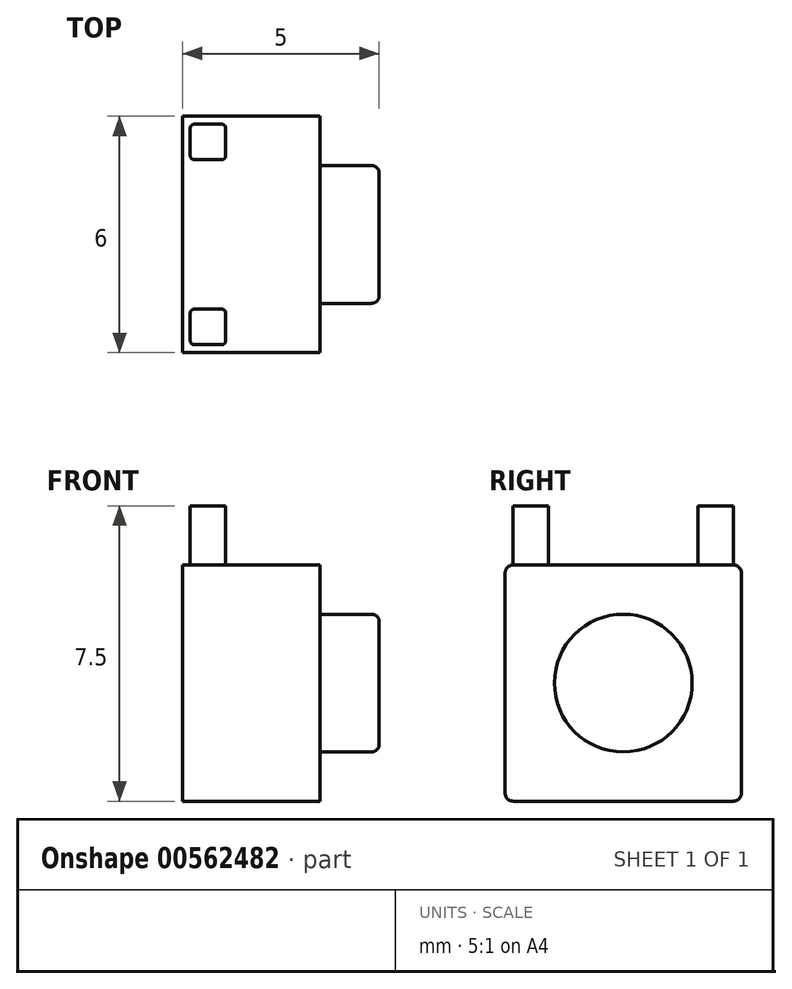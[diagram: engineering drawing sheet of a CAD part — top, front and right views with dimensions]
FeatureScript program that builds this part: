
annotation { "Feature Type Name" : "Feature", "Feature Type Description" : "" }
export const myFeature = defineFeature(function(context is Context, id is Id, definition is map)
    precondition{}
    {
        {
            var Q0;
            Q0=qCreatedBy(makeId("Right.planeOp"),FACE);
            var sketch = newSketch(context, id + "F0", { "sketchPlane" : qUnion([Q0])});
            skLineSegment(sketch, "E0.bottom", {"start": v(-3, 3) * mm, "end": v(3, 3) * mm});
            skLineSegment(sketch, "E0.top", {"start": v(-3, -3) * mm, "end": v(3, -3) * mm});
            skLineSegment(sketch, "E0.left", {"start": v(-3, 3) * mm, "end": v(-3, -3) * mm});
            skLineSegment(sketch, "E0.right", {"start": v(3, 3) * mm, "end": v(3, -3) * mm});
            skPoint(sketch, "E0.middle", {"position": v(0, 0) * mm});
            skSolve(sketch);
        }
        {
            var Q0;
            Q0=qSketchRegion(id+"F0",true);
            extrude(context, id + "F1", {"entities" : qUnion([Q0]), "depth" : 3.5 * mm, "offsetDistance" : 25 * mm, "symmetric" : true});
        }
        {
            var Q0;
            Q0=makeQuery(id+"F1.opExtrude","CAP_FACE",FACE,{"disambiguationData":[OSD([sQuery(id+"F0.wireOp",EDGE,"E0.bottom"),sQuery(id+"F0.wireOp",EDGE,"E0.top"),sQuery(id+"F0.wireOp",EDGE,"E0.left"),sQuery(id+"F0.wireOp",EDGE,"E0.right")])],"isStart":false});
            var sketch = newSketch(context, id + "F2", { "sketchPlane" : qUnion([Q0])});
            skCircle(sketch, "E1", {"center": v(0, 0) * mm, "radius": 1.75 * mm});
            skSolve(sketch);
        }
        {
            var Q0;
            Q0=makeQuery(id+"F2.imprint","IMPRINT",FACE,{"disambiguationData":[TD([[makeQuery(id+"F2.imprint","IMPRINT",EDGE,{"derivedFrom":sQuery(id+"F2.wireOp",EDGE,"E1")}),1.0]])]});
            extrude(context, id + "F3", {"entities" : qUnion([Q0]), "operationType" : NewBodyOperationType.ADD, "depth" : 1.5 * mm, "offsetDistance" : 25 * mm});
        }
        {
            var Q0;
            Q0=makeQuery(id+"F3.opExtrude","CAP_EDGE",EDGE,{"disambiguationData":[OSD([sQuery(id+"F2.wireOp",EDGE,"E1")])],"isStart":false});
            var Q1;
            Q1=makeQuery(id+"F1.opExtrude","SWEPT_EDGE",EDGE,{"disambiguationData":[OSD([sQuery(id+"F0.wireOp",EDGE,"E0.bottom"),sQuery(id+"F0.wireOp",EDGE,"E0.left")])]});
            var Q2;
            Q2=makeQuery(id+"F1.opExtrude","SWEPT_EDGE",EDGE,{"disambiguationData":[OSD([sQuery(id+"F0.wireOp",EDGE,"E0.bottom"),sQuery(id+"F0.wireOp",EDGE,"E0.right")])]});
            var Q3;
            Q3=makeQuery(id+"F1.opExtrude","SWEPT_EDGE",EDGE,{"disambiguationData":[OSD([sQuery(id+"F0.wireOp",EDGE,"E0.top"),sQuery(id+"F0.wireOp",EDGE,"E0.right")])]});
            var Q4;
            Q4=makeQuery(id+"F1.opExtrude","SWEPT_EDGE",EDGE,{"disambiguationData":[OSD([sQuery(id+"F0.wireOp",EDGE,"E0.top"),sQuery(id+"F0.wireOp",EDGE,"E0.left")])]});
            fillet(context, id + "F4", {"entities" : qUnion([Q0, Q1, Q2, Q3, Q4]), "radius" : .2 * mm, "tangentPropagation" : true, "allowEdgeOverflow" : false});
        }
        {
            var Q0;
            Q0=makeQuery(id+"F1.opExtrude","SWEPT_FACE",FACE,{"disambiguationData":[OSD([sQuery(id+"F0.wireOp",EDGE,"E0.bottom")])]});
            var sketch = newSketch(context, id + "F5", { "sketchPlane" : qUnion([Q0])});
            skLineSegment(sketch, "E2.bottom", {"start": v(-1.45, -2.8) * mm, "end": v(-0.75, -2.8) * mm});
            skLineSegment(sketch, "E2.top", {"start": v(-1.45, -1.9) * mm, "end": v(-0.75, -1.9) * mm});
            skLineSegment(sketch, "E2.left", {"start": v(-1.55, -2.7) * mm, "end": v(-1.55, -2) * mm});
            skLineSegment(sketch, "E2.right", {"start": v(-0.65, -2.7) * mm, "end": v(-0.65, -2) * mm});
            skPoint(sketch, "E3.visualSharp", {"position": v(-1.55, -1.9) * mm});
            skArc(sketch, "E3.filletArc", {"start": v(-1.45, -1.9) * mm, "mid": v(-1.52, -1.93) * mm, "end": v(-1.55, -2) * mm});
            skPoint(sketch, "E4.visualSharp", {"position": v(-0.65, -1.9) * mm});
            skArc(sketch, "E4.filletArc", {"start": v(-0.65, -2) * mm, "mid": v(-0.68, -1.93) * mm, "end": v(-0.75, -1.9) * mm});
            skPoint(sketch, "E5.visualSharp", {"position": v(-0.65, -2.8) * mm});
            skArc(sketch, "E5.filletArc", {"start": v(-0.75, -2.8) * mm, "mid": v(-0.68, -2.77) * mm, "end": v(-0.65, -2.7) * mm});
            skPoint(sketch, "E6.visualSharp", {"position": v(-1.55, -2.8) * mm});
            skArc(sketch, "E6.filletArc", {"start": v(-1.55, -2.7) * mm, "mid": v(-1.52, -2.77) * mm, "end": v(-1.45, -2.8) * mm});
            skArc(sketch, "E7.MirrorCS", {"start": v(-0.75, 2.8) * mm, "mid": v(-0.68, 2.77) * mm, "end": v(-0.65, 2.7) * mm});
            skLineSegment(sketch, "E8.MirrorCS", {"start": v(-1.45, 1.9) * mm, "end": v(-0.75, 1.9) * mm});
            skLineSegment(sketch, "E9.MirrorCS", {"start": v(-1.55, 2.7) * mm, "end": v(-1.55, 2) * mm});
            skArc(sketch, "E10.MirrorCS", {"start": v(-1.55, 2.7) * mm, "mid": v(-1.52, 2.77) * mm, "end": v(-1.45, 2.8) * mm});
            skLineSegment(sketch, "E11.MirrorCS", {"start": v(-0.65, 2.7) * mm, "end": v(-0.65, 2) * mm});
            skLineSegment(sketch, "E12.MirrorCS", {"start": v(-1.45, 2.8) * mm, "end": v(-0.75, 2.8) * mm});
            skArc(sketch, "E13.MirrorCS", {"start": v(-1.45, 1.9) * mm, "mid": v(-1.52, 1.93) * mm, "end": v(-1.55, 2) * mm});
            skArc(sketch, "E14.MirrorCS", {"start": v(-0.65, 2) * mm, "mid": v(-0.68, 1.93) * mm, "end": v(-0.75, 1.9) * mm});
            skPoint(sketch, "E15.MirrorP", {"position": v(-1.55, 1.9) * mm});
            skPoint(sketch, "E16.MirrorP", {"position": v(-0.65, 1.9) * mm});
            skPoint(sketch, "E17.MirrorP", {"position": v(-0.65, 2.8) * mm});
            skPoint(sketch, "E18.MirrorP", {"position": v(-1.55, 2.8) * mm});
            skSolve(sketch);
        }
        {
            var Q0;
            Q0=qSketchRegion(id+"F5",true);
            extrude(context, id + "F6", {"entities" : qUnion([Q0]), "operationType" : NewBodyOperationType.ADD, "depth" : 1.5 * mm, "offsetDistance" : 25 * mm});
        }
    });
